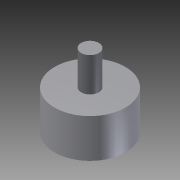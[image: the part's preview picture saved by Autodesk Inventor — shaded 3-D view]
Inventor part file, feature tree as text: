
AUTODESK INVENTOR PART (.ipt)
format: ipt  version: 2012 (Build 160160000, 160)  size: 136,192 bytes
history: native  units: mm
features: extrude x4, sketch x4, other x3, projected_geometry x2, fillet x1
ambient origin geometry x8: Origin, YZ Plane, XZ Plane, XY Plane, X Axis, Y Axis, Z Axis, Center Point
bodies: Solid1 (feature_tree)
feature tree (14):
  other  "ServoToScrewKey.ipt"
  extrude  "Extrusion1"  TaperAngle=0.0deg  [1 undecoded]
  extrude  "Extrusion2"  Depth=20.78461mm
  extrude  "Extrusion3"  Depth=10.0mm TaperAngle=0.0deg
  extrude  "Extrusion5"  Depth=1.0mm
  fillet  "Fillet1"  Radius=4.0mm
  other  "Solid2::ServoToScrewKey.ipt"
  other  "TaggingFeature1"
  sketch  "Sketch2"  dims[d0=10.0mm d1=0.0mm d2=0.0mm]
  projected_geometry  "Projected Loop1"
  sketch  "Sketch3"  dims[d3=12.0mm d4=0.0mm d5=20.78461mm]
  sketch  "Sketch4"  dims[d6=5.196152mm d7=10.0mm d8=0.0mm]
  projected_geometry  "Projected Loop2"
  sketch  "Sketch6"  dims[d20=1.0mm d21=1.0mm d22=4.0mm d23=60.0mm d25=360.0deg d27=10.0mm d28=0.0mm d29=0.5mm]
note: 1 required parameter value undecoded (feature->parameter linkage not recoverable at this tier; creation-order binding heuristic only, values carry confidence <= 0.55)
